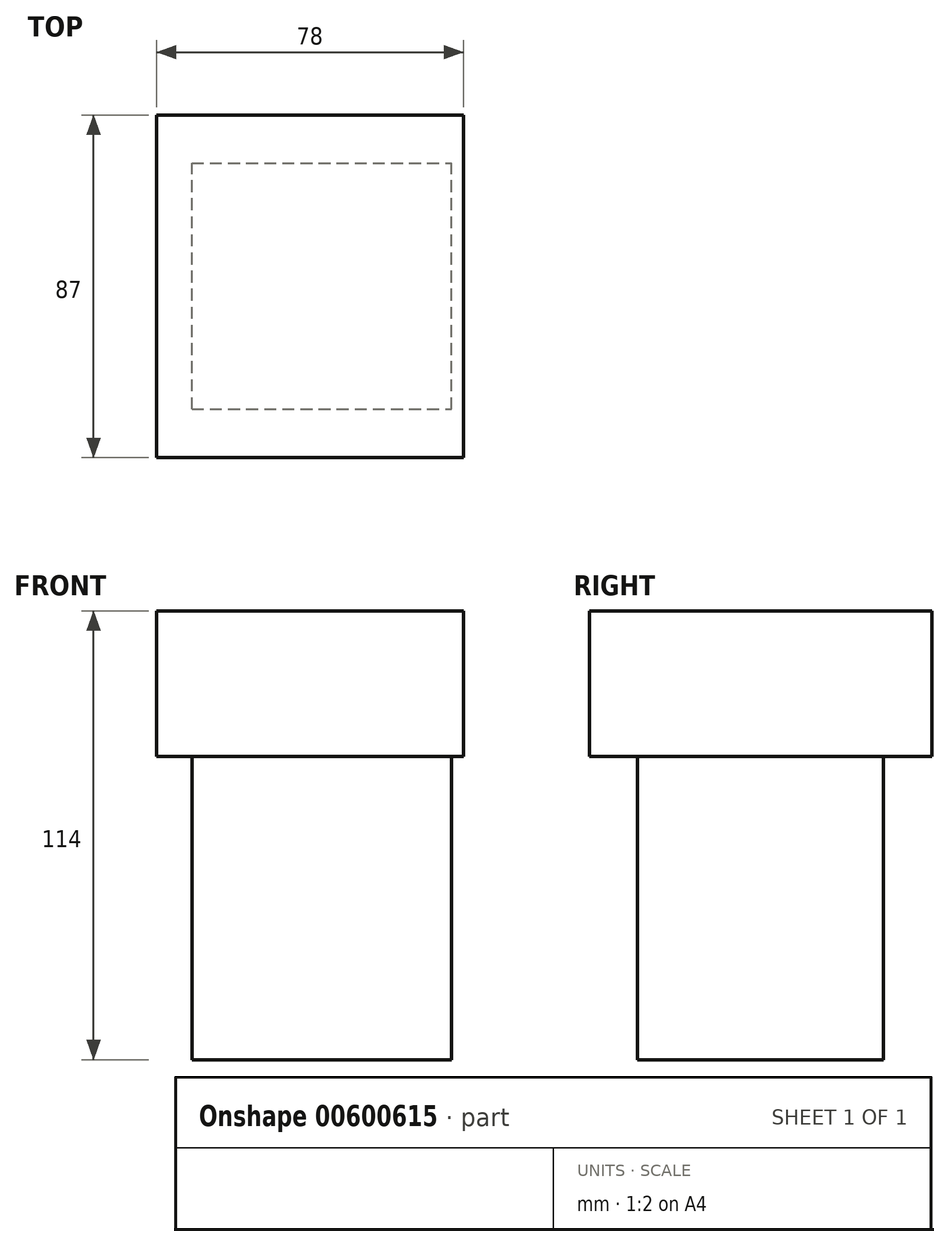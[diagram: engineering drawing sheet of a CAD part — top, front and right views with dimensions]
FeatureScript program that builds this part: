
annotation { "Feature Type Name" : "Feature", "Feature Type Description" : "" }
export const myFeature = defineFeature(function(context is Context, id is Id, definition is map)
    precondition{}
    {
        {
            var Q0;
            Q0=qCreatedBy(makeId("Top.planeOp"),FACE);
            var sketch = newSketch(context, id + "F0", { "sketchPlane" : qUnion([Q0])});
            skLineSegment(sketch, "E0.bottom", {"start": v(-44.64, 49.11) * mm, "end": v(42.36, 49.11) * mm});
            skLineSegment(sketch, "E0.top", {"start": v(-44.64, -28.89) * mm, "end": v(42.36, -28.89) * mm});
            skLineSegment(sketch, "E0.left", {"start": v(-44.64, 49.11) * mm, "end": v(-44.64, -28.89) * mm});
            skLineSegment(sketch, "E0.right", {"start": v(42.36, 49.11) * mm, "end": v(42.36, -28.89) * mm});
            skLineSegment(sketch, "E1.bottom", {"start": v(-32.4, 40.11) * mm, "end": v(30.1, 40.11) * mm});
            skLineSegment(sketch, "E1.top", {"start": v(-32.4, -25.89) * mm, "end": v(30.1, -25.89) * mm});
            skLineSegment(sketch, "E1.left", {"start": v(-32.4, 40.11) * mm, "end": v(-32.4, -25.89) * mm});
            skLineSegment(sketch, "E1.right", {"start": v(30.1, 40.11) * mm, "end": v(30.1, -25.89) * mm});
            skSolve(sketch);
        }
        {
            var Q0;
            Q0 = qSketchRegion(id + "F0", true);
            var Q1;
            Q1=makeQuery(id+"F0.imprint","IMPRINT",FACE,{"disambiguationData":[TD([[makeQuery(id+"F0.imprint","IMPRINT",EDGE,{"derivedFrom":sQuery(id+"F0.wireOp",EDGE,"E1.bottom")}),-1.0]])]});
            extrude(context, id + "F1", {"entities" : qUnion([Q0, Q1]), "depth" : 37 * mm, "offsetDistance" : 25 * mm});
        }
        {
            var Q0;
            Q0=makeQuery(id+"F0.imprint","IMPRINT",FACE,{"disambiguationData":[TD([[makeQuery(id+"F0.imprint","IMPRINT",EDGE,{"derivedFrom":sQuery(id+"F0.wireOp",EDGE,"E1.bottom")}),-1.0]])]});
            extrude(context, id + "F2", {"entities" : qUnion([Q0]), "operationType" : NewBodyOperationType.ADD, "oppositeDirection" : true, "depth" : 77 * mm, "offsetDistance" : 25 * mm});
        }
        {
            var Q0;
            Q0=makeQuery(id+"F1.opExtrude","SWEPT_BODY",BODY,{"disambiguationData":[OSD([sQuery(id+"F0.wireOp",EDGE,"E0.bottom"),sQuery(id+"F0.wireOp",EDGE,"E0.top"),sQuery(id+"F0.wireOp",EDGE,"E0.left"),sQuery(id+"F0.wireOp",EDGE,"E0.right")])]});
            var Q1;
            Q1=makeQuery(id+"F2.opExtrude","SWEPT_EDGE",EDGE,{"disambiguationData":[OSD([sQuery(id+"F0.wireOp",EDGE,"E1.top"),sQuery(id+"F0.wireOp",EDGE,"E1.left")])]});
            transform(context, id + "F3", {"entities" : qUnion([Q0]), "transformType" : TransformType.ROTATION, "transformAxis" : qUnion([Q1]), "angle" : 90 * degree, "makeCopy" : false});
        }
    });
